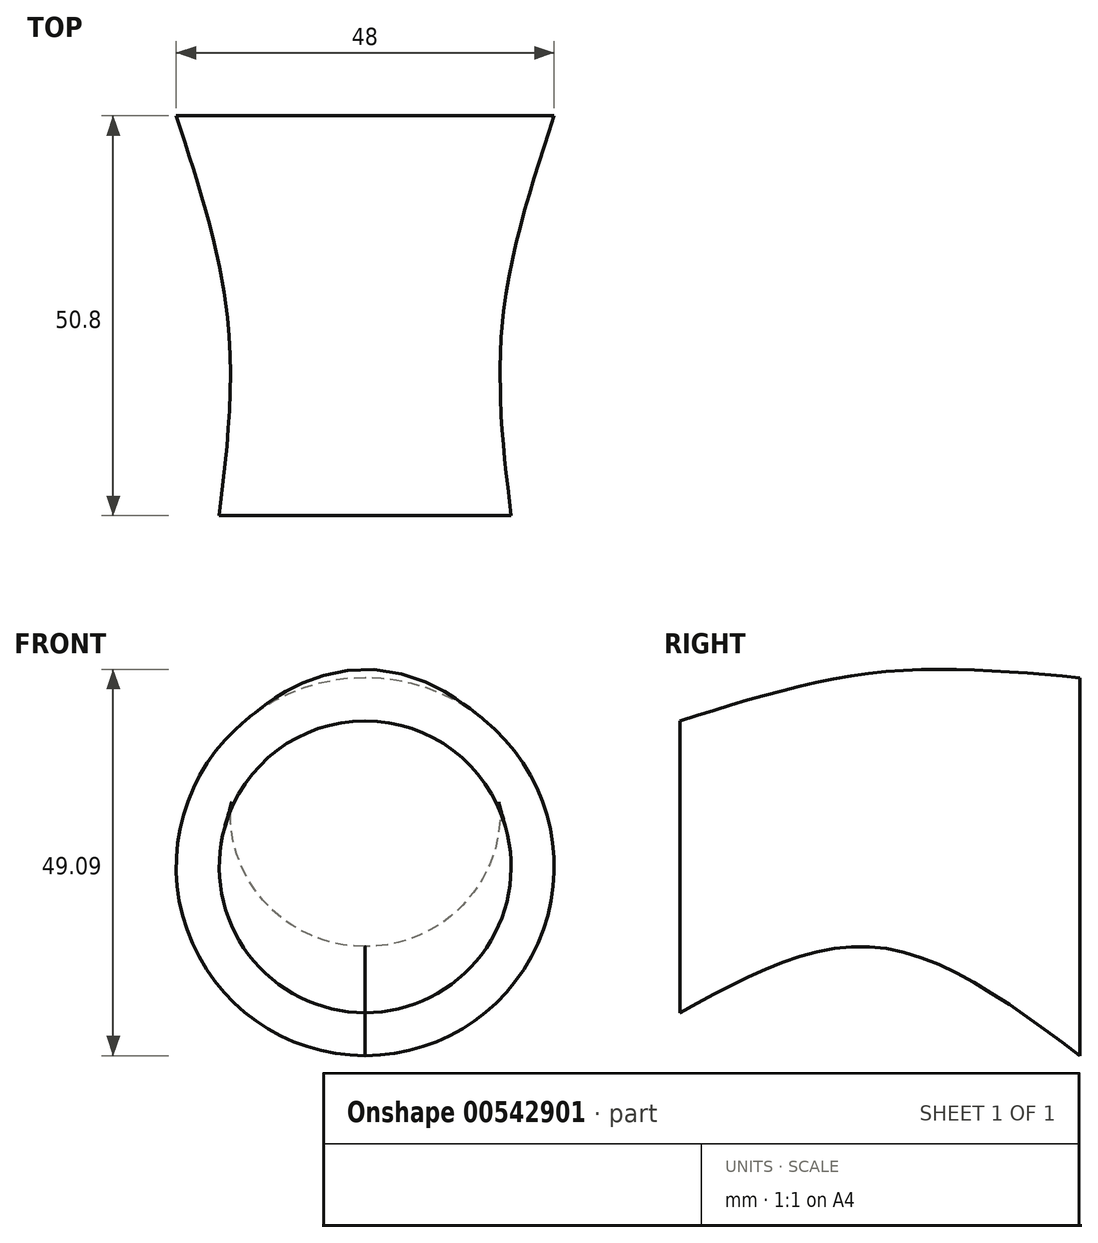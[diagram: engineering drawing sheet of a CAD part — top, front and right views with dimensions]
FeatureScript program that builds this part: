
annotation { "Feature Type Name" : "Feature", "Feature Type Description" : "" }
export const myFeature = defineFeature(function(context is Context, id is Id, definition is map)
    precondition{}
    {
        {
            var Q0;
            Q0=qCreatedBy(makeId("Front.planeOp"),FACE);
            var sketch = newSketch(context, id + "F0", { "sketchPlane" : qUnion([Q0])});
            skCircle(sketch, "E0", {"center": v(0, 0) * mm, "radius": 24 * mm});
            skSolve(sketch);
        }
        {
            var Q0;
            Q0=qCreatedBy(makeId("Front.planeOp"),FACE);
            cPlane(context, id + "F1", {"entities" : qUnion([Q0]), "cplaneType" : CPlaneType.OFFSET, "offset" : 25.4 * mm, "width" : 152.4 * mm, "height" : 152.4 * mm});
        }
        {
            var Q0;
            Q0=qCreatedBy(id+"F1.planeOp",FACE);
            cPlane(context, id + "F2", {"entities" : qUnion([Q0]), "cplaneType" : CPlaneType.OFFSET, "offset" : 25.4 * mm, "width" : 152.4 * mm, "height" : 152.4 * mm});
        }
        {
            var Q0;
            Q0=qCreatedBy(id+"F1.planeOp",FACE);
            var sketch = newSketch(context, id + "F3", { "sketchPlane" : qUnion([Q0])});
            skCircle(sketch, "E1", {"center": v(0, 7.21) * mm, "radius": 17.5 * mm});
            skSolve(sketch);
        }
        {
            var Q0;
            Q0=qCreatedBy(id+"F2.planeOp",FACE);
            var sketch = newSketch(context, id + "F4", { "sketchPlane" : qUnion([Q0])});
            skCircle(sketch, "E2", {"center": v(0, 0) * mm, "radius": 18.53 * mm});
            skSolve(sketch);
        }
        {
            var Q0;
            Q0=makeQuery(id+"F0.imprint","IMPRINT",FACE,{"disambiguationData":[TD([[makeQuery(id+"F0.imprint","IMPRINT",EDGE,{"derivedFrom":sQuery(id+"F0.wireOp",EDGE,"E0")}),1.0]])]});
            var Q1;
            Q1=makeQuery(id+"F3.imprint","IMPRINT",FACE,{"disambiguationData":[TD([[makeQuery(id+"F3.imprint","IMPRINT",EDGE,{"derivedFrom":sQuery(id+"F3.wireOp",EDGE,"E1")}),1.0]])]});
            var Q2;
            Q2=makeQuery(id+"F4.imprint","IMPRINT",FACE,{"disambiguationData":[TD([[makeQuery(id+"F4.imprint","IMPRINT",EDGE,{"derivedFrom":sQuery(id+"F4.wireOp",EDGE,"E2")}),1.0]])]});
            loft(context, id + "F5", {"sheetProfilesArray" : [{ "sheetProfileEntities" : qUnion([Q0]) }, { "sheetProfileEntities" : qUnion([Q1]) }, { "sheetProfileEntities" : qUnion([Q2]) }]});
        }
    });
